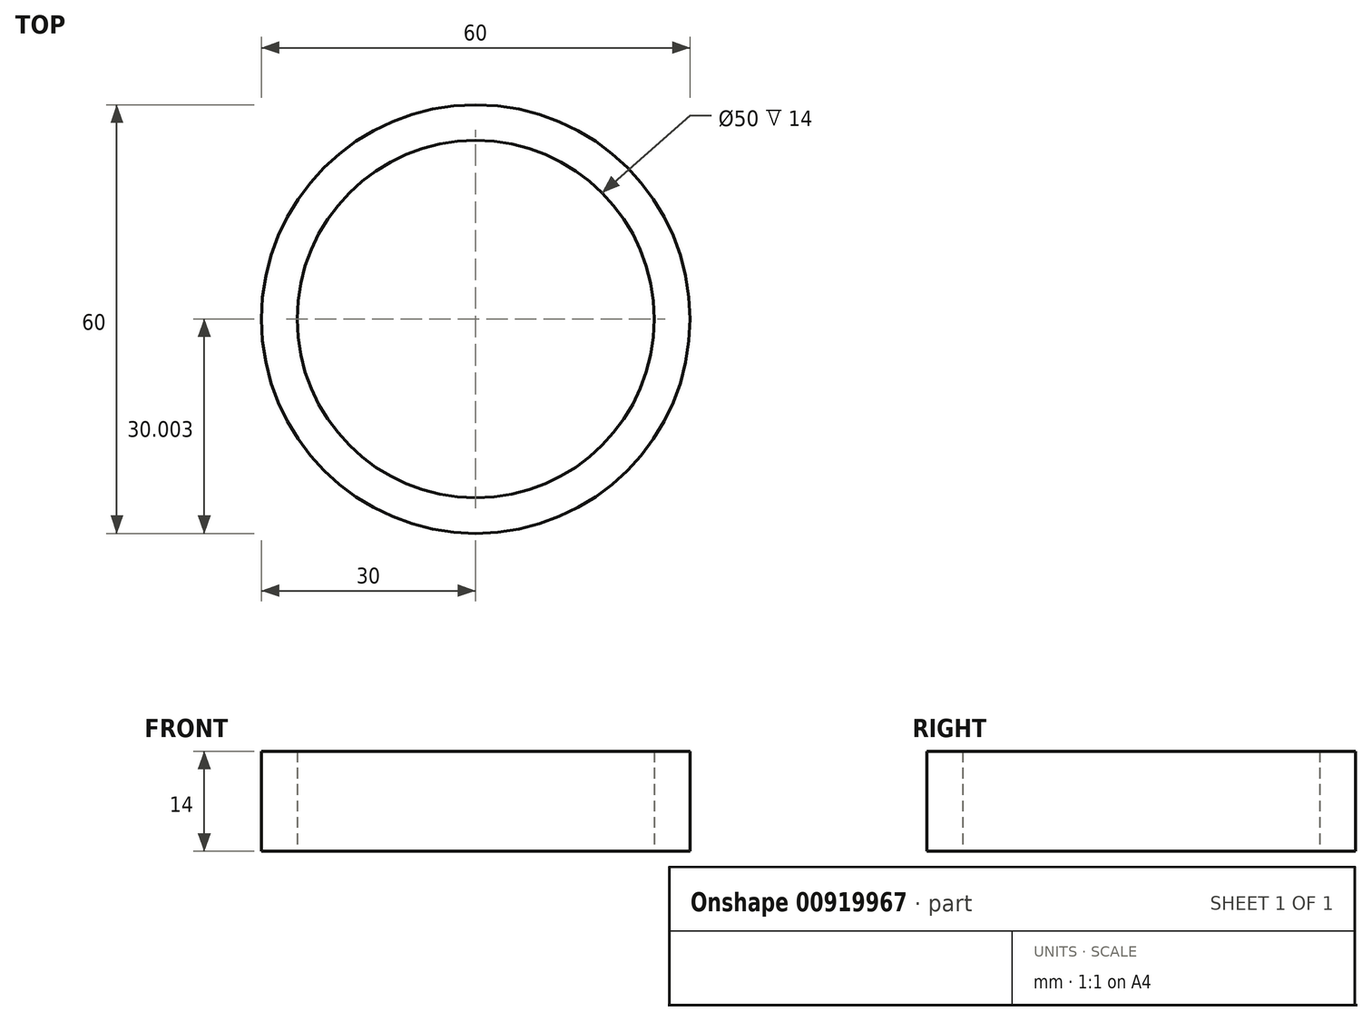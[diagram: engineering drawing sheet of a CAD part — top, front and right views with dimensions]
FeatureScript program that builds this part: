
annotation { "Feature Type Name" : "Feature", "Feature Type Description" : "" }
export const myFeature = defineFeature(function(context is Context, id is Id, definition is map)
    precondition{}
    {
        {
            var Q0;
            Q0=qCreatedBy(makeId("Top.planeOp"),FACE);
            var sketch = newSketch(context, id + "F0", { "sketchPlane" : qUnion([Q0])});
            skCircle(sketch, "E0", {"center": v(-60.08, -45.73) * mm, "radius": 25 * mm});
            skCircle(sketch, "E1", {"center": v(-60.08, -45.73) * mm, "radius": 30 * mm});
            skSolve(sketch);
        }
        {
            var Q0;
            Q0 = qSketchRegion(id + "F0", true);
            extrude(context, id + "F1", {"entities" : qUnion([Q0]), "depth" : 14 * mm, "offsetDistance" : 25 * mm});
        }
    });
